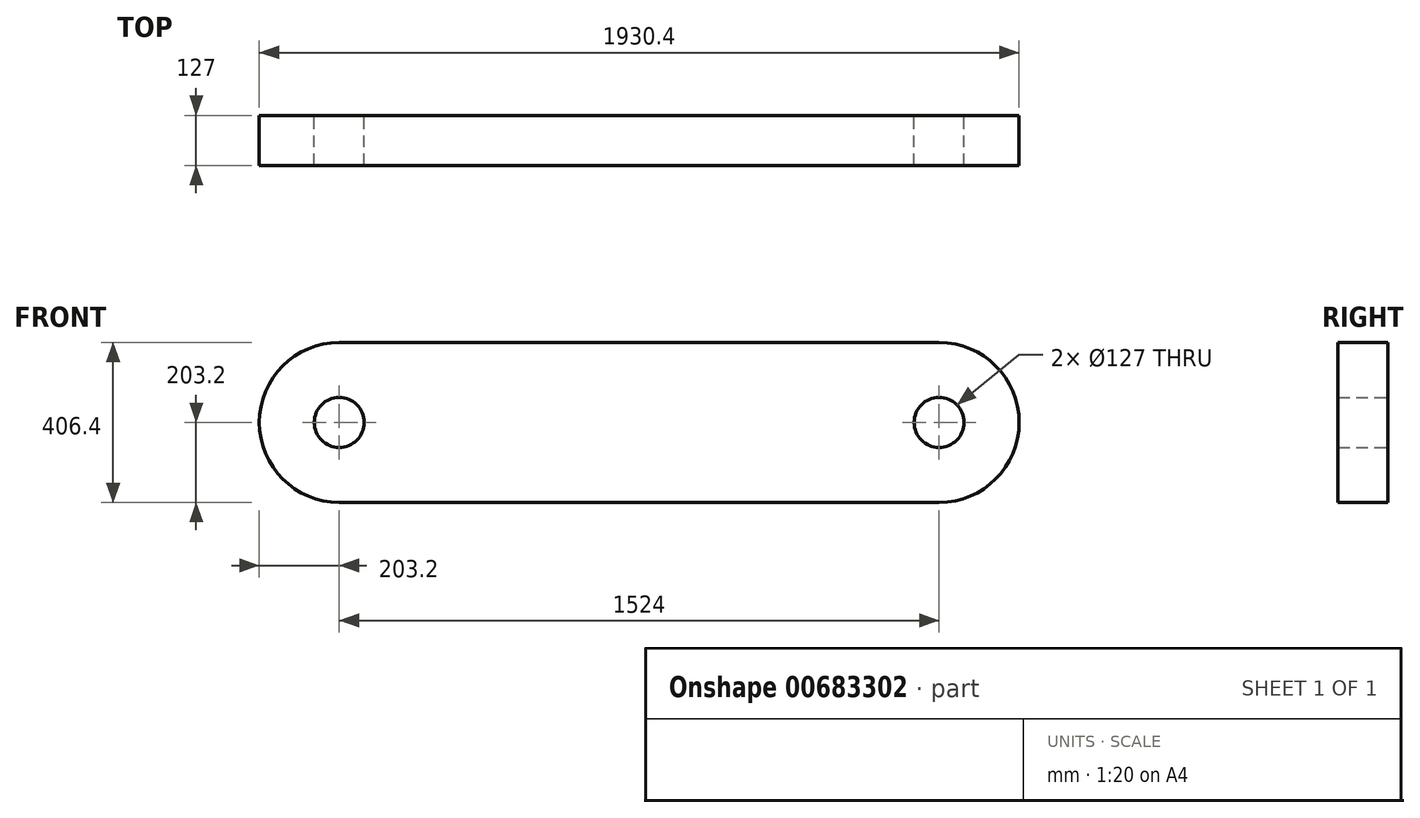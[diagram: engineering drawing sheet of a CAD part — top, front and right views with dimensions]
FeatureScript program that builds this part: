
annotation { "Feature Type Name" : "Feature", "Feature Type Description" : "" }
export const myFeature = defineFeature(function(context is Context, id is Id, definition is map)
    precondition{}
    {
        {
            var Q0;
            Q0=qCreatedBy(makeId("Front.planeOp"),FACE);
            var sketch = newSketch(context, id + "F0", { "sketchPlane" : qUnion([Q0])});
            skLineSegment(sketch, "E0.bottom", {"start": v(-762, 203.2) * mm, "end": v(762, 203.2) * mm});
            skLineSegment(sketch, "E0.top", {"start": v(-762, -203.2) * mm, "end": v(762, -203.2) * mm});
            skArc(sketch, "E1", {"start": v(-762, 203.2) * mm, "mid": v(-965.2, 0) * mm, "end": v(-762, -203.2) * mm});
            skArc(sketch, "E2", {"start": v(762, -203.2) * mm, "mid": v(965.2, 0) * mm, "end": v(762, 203.2) * mm});
            skCircle(sketch, "E3", {"center": v(-762, 0) * mm, "radius": 63.5 * mm});
            skCircle(sketch, "E4", {"center": v(762, 0) * mm, "radius": 63.5 * mm});
            skSolve(sketch);
        }
        {
            var Q0;
            Q0=qSketchRegion(id+"F0",true);
            extrude(context, id + "F1", {"entities" : qUnion([Q0]), "depth" : 127 * mm, "offsetDistance" : 25.4 * mm});
        }
    });
